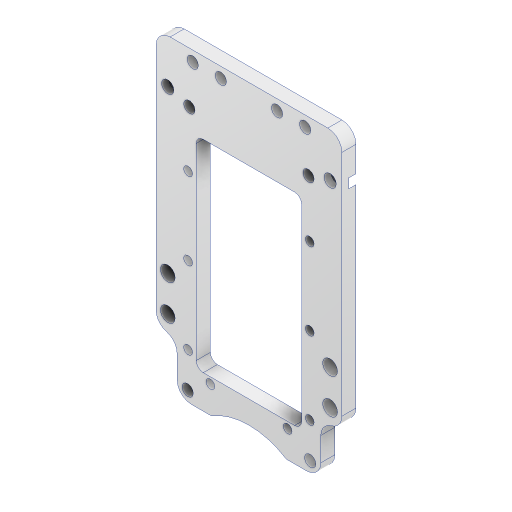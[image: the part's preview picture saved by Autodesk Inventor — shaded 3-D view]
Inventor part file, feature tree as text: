
AUTODESK INVENTOR PART (.ipt)
format: ipt  version: 2023.2 (Build 272271000, 271)  size: 409,088 bytes
history: native  units: mm
features: sketch x9, extrude x8, projected_geometry x4, fillet x1
ambient origin geometry x8: Origin, YZ Plane, XZ Plane, XY Plane, X Axis, Y Axis, Z Axis, Center Point
bodies: Body1 (feature_tree)
feature tree (22):
  sketch  "스케치1"
  extrude  "돌출2"  Depth=62.0mm
  sketch  "스케치4"
  extrude  "돌출4"  Depth=5.6mm
  extrude  "돌출3"  Depth=1.0mm
  extrude  "돌출5"  Depth=0.5mm
  extrude  "돌출8"  Depth=0.5mm
  extrude  "돌출9"  Depth=1.0mm
  extrude  "돌출10"  Depth=3.7mm
  fillet  "모깎기7"  Radius=3.699999mm
  extrude  "돌출12"  Depth=68.5mm
  sketch  "스케치5"
  projected_geometry  "투영된 루프1"
  sketch  "스케치7"
  sketch  "스케치8"
  sketch  "스케치12"
  sketch  "스케치13"
  projected_geometry  "투영된 루프2"
  sketch  "스케치14"
  projected_geometry  "투영된 루프3"
  sketch  "스케치18"
  projected_geometry  "투영된 루프7"
